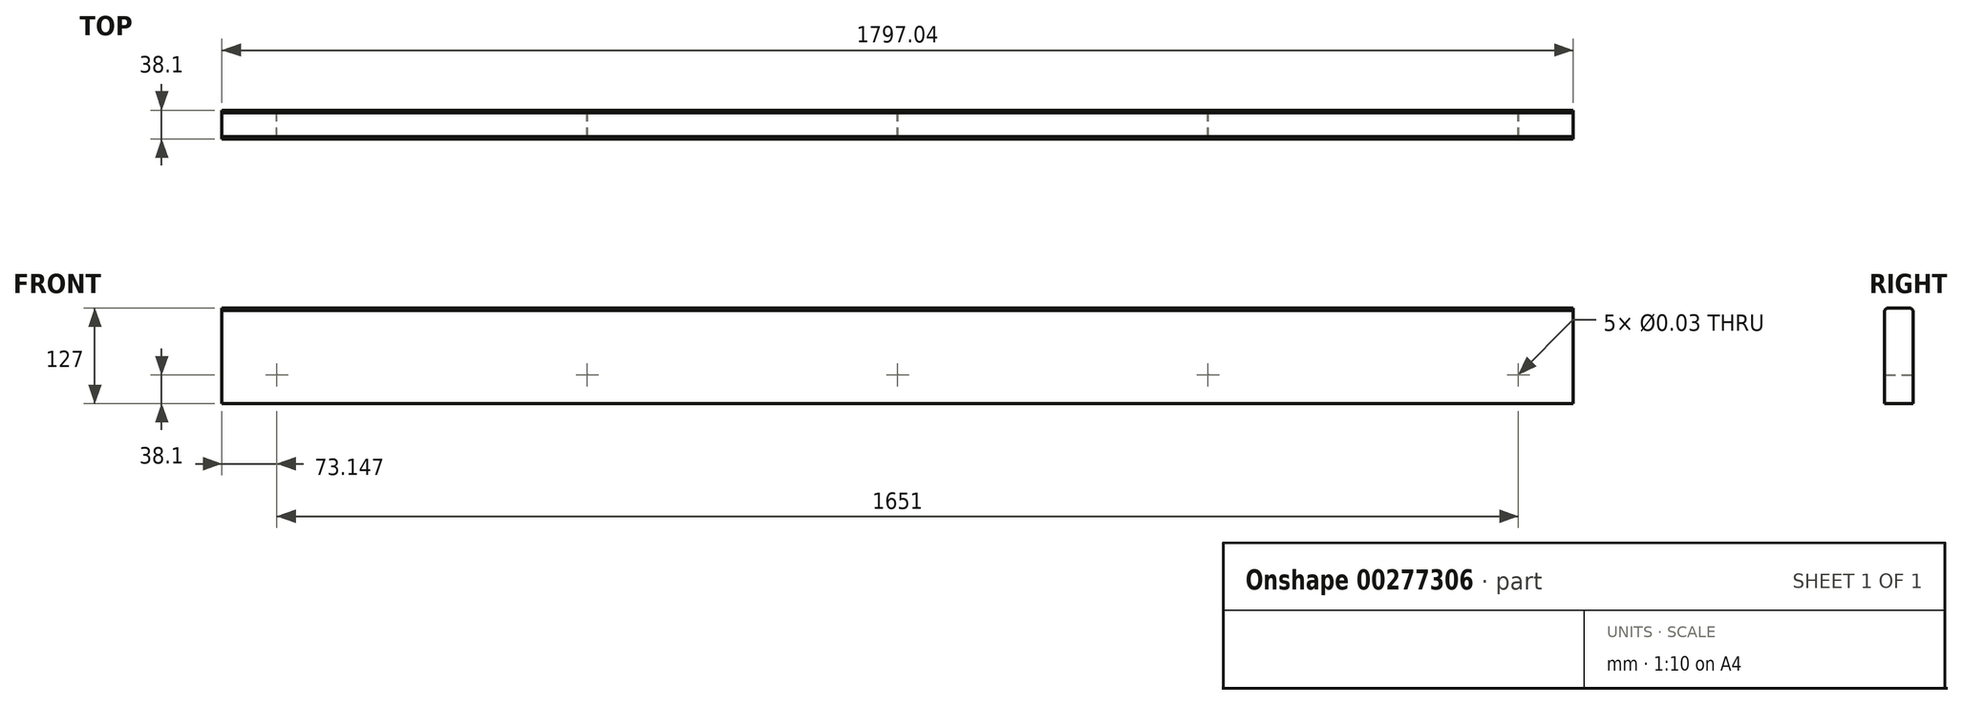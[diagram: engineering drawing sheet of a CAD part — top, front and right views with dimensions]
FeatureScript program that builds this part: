
annotation { "Feature Type Name" : "Feature", "Feature Type Description" : "" }
export const myFeature = defineFeature(function(context is Context, id is Id, definition is map)
    precondition{}
    {
        {
            var Q0;
            Q0=qCreatedBy(makeId("Right.planeOp"),FACE);
            var sketch = newSketch(context, id + "F0", { "sketchPlane" : qUnion([Q0])});
            skLineSegment(sketch, "E0.bottom", {"start": v(-19.05, 63.5) * mm, "end": v(19.05, 63.5) * mm});
            skLineSegment(sketch, "E0.top", {"start": v(-19.05, -63.5) * mm, "end": v(19.05, -63.5) * mm});
            skLineSegment(sketch, "E0.left", {"start": v(-19.05, 63.5) * mm, "end": v(-19.05, -63.5) * mm});
            skLineSegment(sketch, "E0.right", {"start": v(19.05, 63.5) * mm, "end": v(19.05, -63.5) * mm});
            skPoint(sketch, "E0.middle", {"position": v(0, 0) * mm});
            skSolve(sketch);
        }
        {
            var Q0;
            Q0=qSketchRegion(id+"F0",true);
            extrude(context, id + "F1", {"entities" : qUnion([Q0]), "endBound" : BoundingType.SYMMETRIC, "depth" : 1797.05 * mm});
        }
        {
            var Q0;
            Q0=makeQuery(id+"F1.opExtrude","SWEPT_EDGE",EDGE,{"disambiguationData":[OSD([sQuery(id+"F0.wireOp",EDGE,"E0.bottom"),sQuery(id+"F0.wireOp",EDGE,"E0.right")])]});
            var Q1;
            Q1=makeQuery(id+"F1.opExtrude","SWEPT_EDGE",EDGE,{"disambiguationData":[OSD([sQuery(id+"F0.wireOp",EDGE,"E0.bottom"),sQuery(id+"F0.wireOp",EDGE,"E0.left")])]});
            chamfer(context, id + "F2", {"entities" : qUnion([Q0, Q1]), "width" : 3.17 * mm, "tangentPropagation" : true});
        }
        {
            var Q0;
            Q0=makeQuery(id+"F1.opExtrude","SWEPT_FACE",FACE,{"disambiguationData":[OSD([sQuery(id+"F0.wireOp",EDGE,"E0.right")])]});
            var sketch = newSketch(context, id + "F3", { "sketchPlane" : qUnion([Q0])});
            skLineSegment(sketch, "E1.0", {"start": v(-898.53, -63.5) * mm, "end": v(898.53, -63.5) * mm, "construction": true});
            skLineSegment(sketch, "E2.0", {"start": v(-898.53, -25.4) * mm, "end": v(898.53, -25.4) * mm, "construction": true});
            skLineSegment(sketch, "E3.0", {"start": v(-898.53, 60.33) * mm, "end": v(-898.53, -63.5) * mm, "construction": true});
            skLineSegment(sketch, "E4.0", {"start": v(-825.63, 60.33) * mm, "end": v(-825.63, -63.5) * mm, "construction": true});
            skPoint(sketch, "E5", {"position": v(-825.63, -25.4) * mm});
            skPoint(sketch, "E6.1.0.0", {"position": v(-412.88, -25.4) * mm});
            skPoint(sketch, "E6.2.0.0", {"position": v(-0.13, -25.4) * mm});
            skPoint(sketch, "E6.3.0.0", {"position": v(412.62, -25.4) * mm});
            skPoint(sketch, "E6.4.0.0", {"position": v(825.37, -25.4) * mm});
            skLineSegment(sketch, "E6.direction1", {"start": v(-825.63, -25.4) * mm, "end": v(-412.88, -25.4) * mm, "construction": true});
            skSolve(sketch);
        }
        {
            var Q0;
            Q0=sQuery(id+"F3.wireOp",VERTEX,"E5");
            var Q1;
            Q1=sQuery(id+"F3.wireOp",VERTEX,"E6.1.0.0");
            var Q2;
            Q2=sQuery(id+"F3.wireOp",VERTEX,"E6.2.0.0");
            var Q3;
            Q3=sQuery(id+"F3.wireOp",VERTEX,"E6.3.0.0");
            var Q4;
            Q4=sQuery(id+"F3.wireOp",VERTEX,"E6.4.0.0");
            var Q5;
            Q5=makeQuery(id+"F1.opExtrude","SWEPT_BODY",BODY,{"disambiguationData":[OSD([sQuery(id+"F0.wireOp",EDGE,"E0.bottom"),sQuery(id+"F0.wireOp",EDGE,"E0.top"),sQuery(id+"F0.wireOp",EDGE,"E0.left"),sQuery(id+"F0.wireOp",EDGE,"E0.right")])]});
            hole(context, id + "F4", {"style" : HoleStyle.SIMPLE, "endStyle" : HoleEndStyle.THROUGH, "standardTappedOrClearance" : lookupTablePath({ "standard" : "ANSI", "size" : "13/16 (0.81)", "type" : "Drilled" }), "standardBlindInLast" : lookupTablePath({ "standard" : "ANSI", "size" : "13/16", "type" : "Drilled" }), "holeDiameter" : 13 / 406.4 * mm, "tappedDepth" : 41.27 * mm, "tapClearance" : 3, "startFromSketch" : true, "locations" : qUnion([Q0, Q1, Q2, Q3, Q4]), "scope" : qUnion([Q5])});
        }
    });
